# Revit family: HERZ Shut-off valve 4125 D
name_source: partatom
category: Rohrzubehör
revit_build: Autodesk Revit 2018 (Build: 20190510_1515(x64)
units: mm (PartAtom-declared; Revit-internal decimal feet)

## family parameters
Arbeitsebenenbasiert = Nein
Beim Laden mit Abzugskörper schneiden = Nein
Bemaßung runder Anschluss = Durchmesser verwenden
Gemeinsam genutzt = Nein
Immer vertikal = Ja
OmniClass-Nummer = 23.65.55.14
OmniClass-Titel = Valves for Liquid Services
Teiletyp = Unterbricht

## types (1)
- HERZ Shut-off valve 4125 D
    Application = Reliable shutting of pipes in heating and cooling systems.
    Body = casted DZR brass CC752S
    Cone = DZR brass CW602N
    Hand wheel = Polyamide
    Hersteller = HERZ Armaturen Ges.m.b.H.
    L03 = 15 mm
    Max. differential pressure on closed seat = 1000000.0 Pa
    Max. operating pressure = 2000000.0 Pa
    Max. operating temperature = 110 °C
    Medium = Heating water according ÖNORM H5195 or VDI- Standard 2035.
The use of ethylene- or propylene glycol in a mixing ratio 25- 50% is allowed.
    Model = STRÖMAX-D shut-off valve, inclined model, brass version, socket x socket,
with long threaded sockets, non-rising spindle,
spindle sealing by means of elastic double-O-ring.
    R03 = 9.5 mm  [stored 0.031168 ft]
    R100 = 1 mm  [stored 0.00328084 ft]
    S03 = 60 mm  [stored 0.19685 ft]
    SCRNCODE = 05;07;02
    SCRNSEQ = ARM;ARM_TYP="ABSV";2
    SW01 = 60.00°
    Sealing = EPDM
    Spindle = brass CW617N
    URL = www.herzvalves.com
    Upper part = DZR brass CW602N
    W01 = 45.00°

note: [stored X ft] marks values corroborated as IEEE doubles in the binary element streams (Revit-internal decimal feet)
